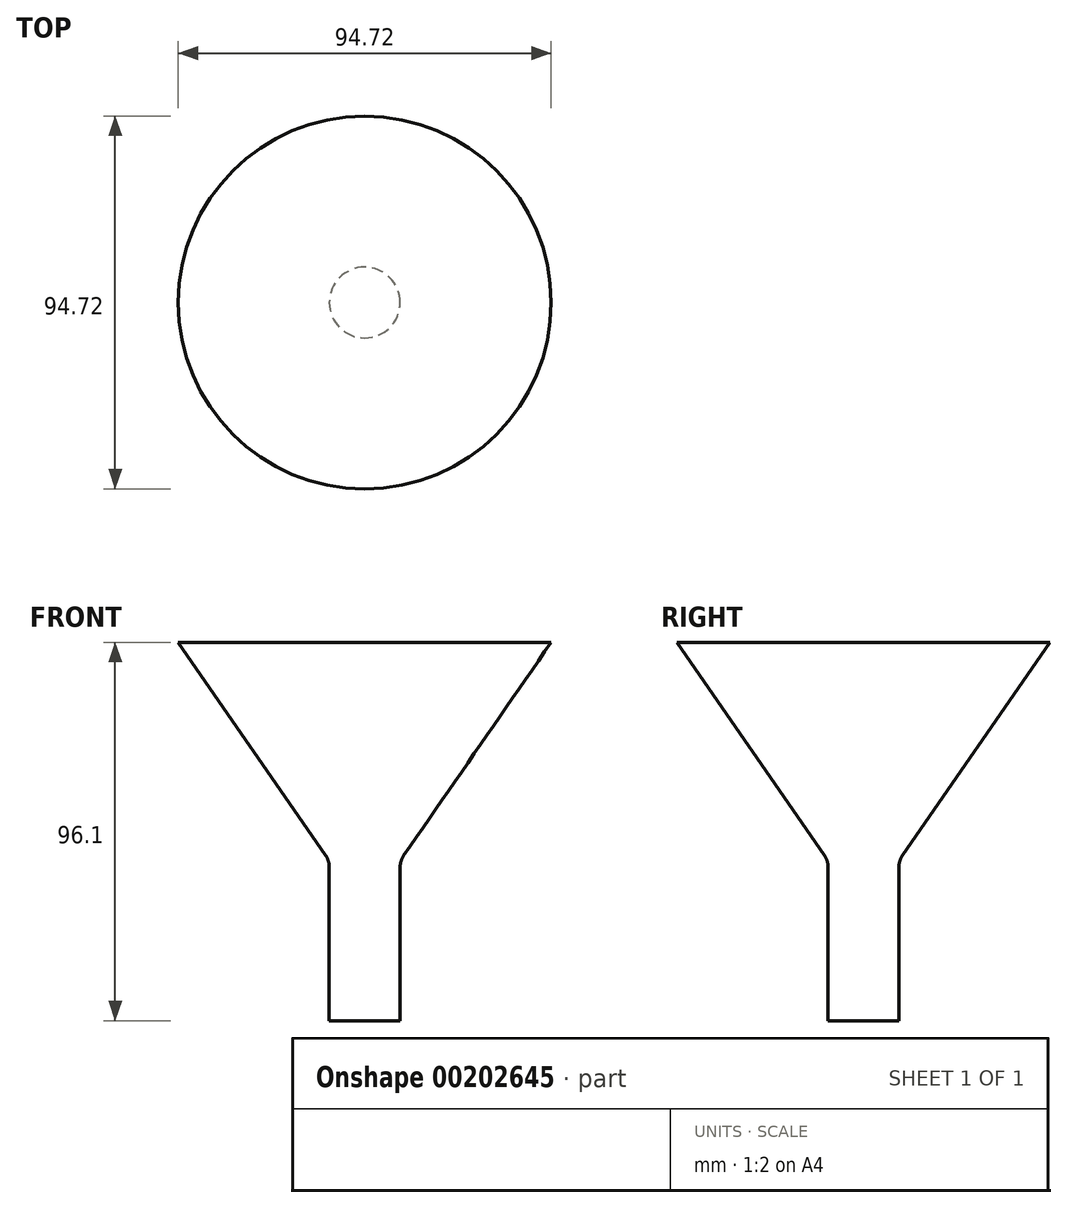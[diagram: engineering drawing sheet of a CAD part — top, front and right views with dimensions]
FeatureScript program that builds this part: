
annotation { "Feature Type Name" : "Feature", "Feature Type Description" : "" }
export const myFeature = defineFeature(function(context is Context, id is Id, definition is map)
    precondition{}
    {
        {
            var Q0;
            Q0=qCreatedBy(makeId("Front.planeOp"),FACE);
            var sketch = newSketch(context, id + "F0", { "sketchPlane" : qUnion([Q0])});
            skLineSegment(sketch, "E0", {"start": v(0, 40) * mm, "end": v(-9, 40) * mm});
            skLineSegment(sketch, "E1", {"start": v(-9, 40) * mm, "end": v(-9, 79.09) * mm});
            skLineSegment(sketch, "E2", {"start": v(-47.36, 136.1) * mm, "end": v(-9.89, 81.93) * mm});
            skPoint(sketch, "E3.visualSharp", {"position": v(-9, 80.65) * mm});
            skArc(sketch, "E3.filletArc", {"start": v(-9, 79.09) * mm, "mid": v(-9.23, 80.58) * mm, "end": v(-9.89, 81.93) * mm});
            skLineSegment(sketch, "E4", {"start": v(-47.36, 136.1) * mm, "end": v(0, 136.1) * mm});
            skLineSegment(sketch, "E5", {"start": v(0, 136.1) * mm, "end": v(0, 40) * mm});
            skSolve(sketch);
        }
        {
            var Q0;
            Q0=qCreatedBy(makeId("Front.planeOp"),FACE);
            var sketch = newSketch(context, id + "F1", { "sketchPlane" : qUnion([Q0])});
            skLineSegment(sketch, "E6", {"start": v(0, 143.98) * mm, "end": v(0, 20.44) * mm, "construction": true});
            skSolve(sketch);
        }
        {
            var Q0;
            Q0 = qSketchRegion(id + "F0", true);
            var Q1;
            Q1=sQuery(id+"F1.wireOp",EDGE,"E6");
            revolve(context, id + "F2", {"entities" : qUnion([Q0]), "axis" : qUnion([Q1]), "revolveType" : RevolveType.FULL});
        }
    });
